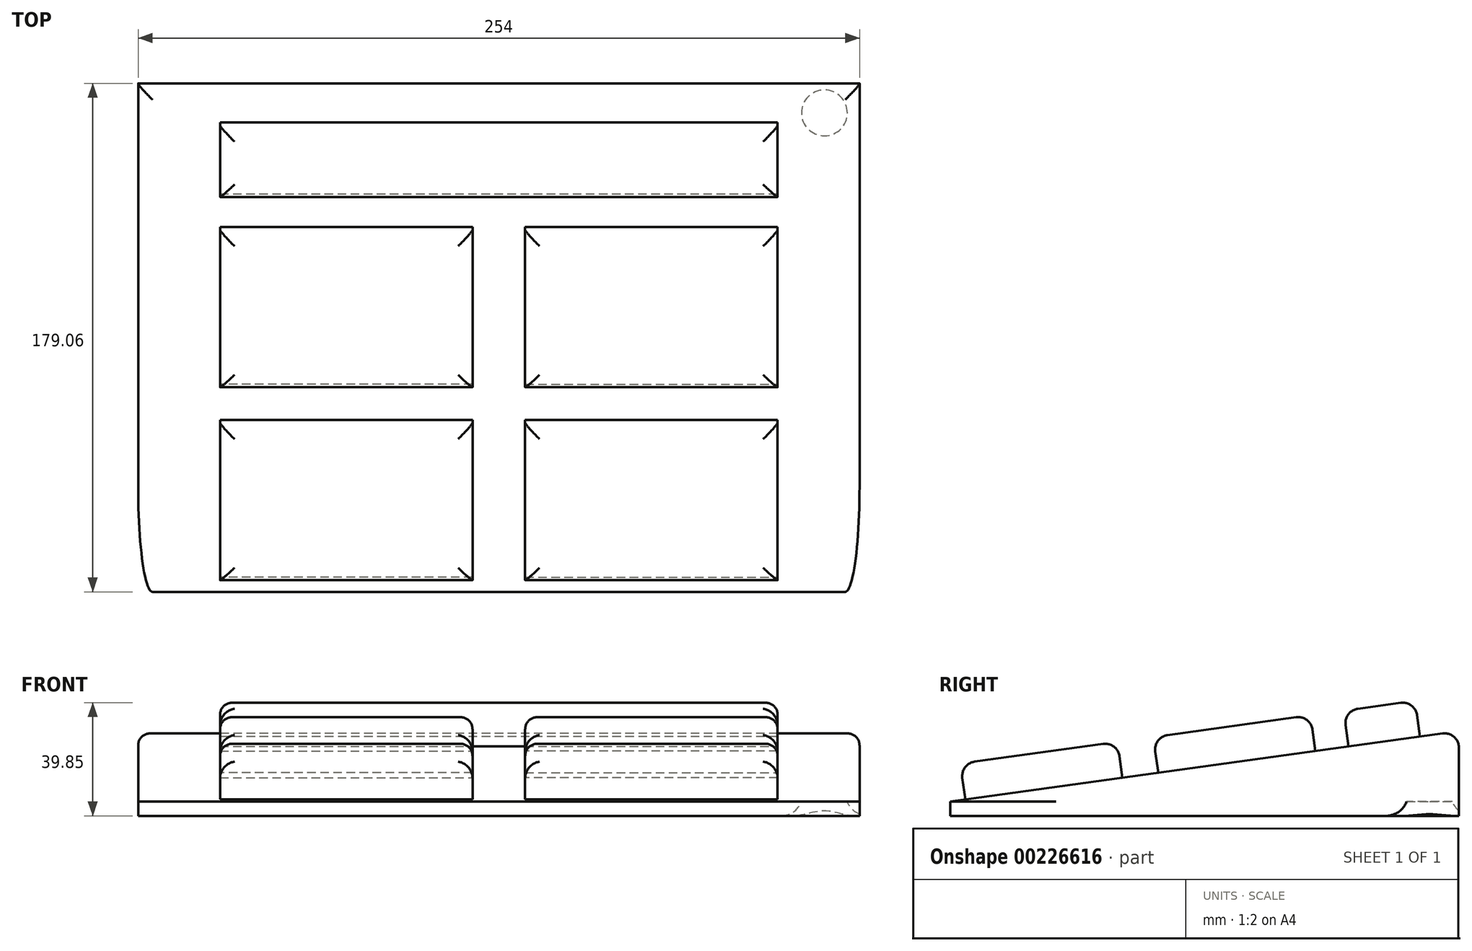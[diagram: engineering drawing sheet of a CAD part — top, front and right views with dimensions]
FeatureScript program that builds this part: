
annotation { "Feature Type Name" : "Feature", "Feature Type Description" : "" }
export const myFeature = defineFeature(function(context is Context, id is Id, definition is map)
    precondition{}
    {
        {
            var Q0;
            Q0=qCreatedBy(makeId("Right.planeOp"),FACE);
            var sketch = newSketch(context, id + "F0", { "sketchPlane" : qUnion([Q0])});
            skLineSegment(sketch, "E0", {"start": v(102.27, 24.73) * mm, "end": v(102.27, 0) * mm});
            skLineSegment(sketch, "E1", {"start": v(102.27, 0) * mm, "end": v(-76.8, 0) * mm});
            skLineSegment(sketch, "E2", {"start": v(-76.8, 0) * mm, "end": v(102.27, 24.73) * mm});
            skSolve(sketch);
        }
        {
            var Q0;
            Q0 = qSketchRegion(id + "F0", true);
            extrude(context, id + "F1", {"entities" : qUnion([Q0]), "endBound" : BoundingType.SYMMETRIC, "depth" : 254 * mm});
        }
        {
            var Q0;
            Q0=makeQuery(id+"F1.opExtrude","CAP_EDGE",EDGE,{"disambiguationData":[OSD([sQuery(id+"F0.wireOp",EDGE,"E2")])],"isStart":true});
            var Q1;
            Q1=makeQuery(id+"F1.opExtrude","CAP_EDGE",EDGE,{"disambiguationData":[OSD([sQuery(id+"F0.wireOp",EDGE,"E2")])],"isStart":false});
            var Q2;
            Q2=makeQuery(id+"F1.opExtrude","SWEPT_EDGE",EDGE,{"disambiguationData":[OSD([sQuery(id+"F0.wireOp",EDGE,"E0"),sQuery(id+"F0.wireOp",EDGE,"E2")])]});
            fillet(context, id + "F2", {"entities" : qUnion([Q0, Q1, Q2]), "radius" : 5.08 * mm, "tangentPropagation" : true, "allowEdgeOverflow" : false});
        }
        {
            var Q0;
            Q0=makeQuery(id+"F1.opExtrude","SWEPT_FACE",FACE,{"disambiguationData":[OSD([sQuery(id+"F0.wireOp",EDGE,"E2")])]});
            var sketch = newSketch(context, id + "F3", { "sketchPlane" : qUnion([Q0])});
            skLineSegment(sketch, "E3", {"start": v(0, 62.96) * mm, "end": v(0, -67.39) * mm, "construction": true});
            skLineSegment(sketch, "E4", {"start": v(-9.26, -2.21) * mm, "end": v(-98.16, -2.21) * mm});
            skPoint(sketch, "E4.startSnap0", {"position": v(0, -2.21) * mm});
            skLineSegment(sketch, "E5", {"start": v(-98.16, -2.21) * mm, "end": v(-98.16, 53.67) * mm});
            skLineSegment(sketch, "E6", {"start": v(-98.16, 53.67) * mm, "end": v(-9.26, 53.67) * mm});
            skLineSegment(sketch, "E7", {"start": v(-9.26, 53.67) * mm, "end": v(-9.26, -2.21) * mm});
            skLineSegment(sketch, "E8", {"start": v(-98.16, -14.91) * mm, "end": v(-9.26, -14.91) * mm});
            skLineSegment(sketch, "E9", {"start": v(-9.26, -14.91) * mm, "end": v(-9.26, -70.8) * mm});
            skLineSegment(sketch, "E10", {"start": v(-9.26, -70.8) * mm, "end": v(-98.16, -70.8) * mm});
            skLineSegment(sketch, "E11", {"start": v(-98.16, -70.8) * mm, "end": v(-98.16, -14.91) * mm});
            skLineSegment(sketch, "E12.MirrorCS", {"start": v(98.16, -2.21) * mm, "end": v(98.16, 53.67) * mm});
            skLineSegment(sketch, "E13.MirrorCS", {"start": v(98.16, 53.67) * mm, "end": v(9.26, 53.67) * mm});
            skLineSegment(sketch, "E14.MirrorCS", {"start": v(9.26, 53.67) * mm, "end": v(9.26, -2.21) * mm});
            skLineSegment(sketch, "E15.MirrorCS", {"start": v(9.26, -2.21) * mm, "end": v(98.16, -2.21) * mm});
            skLineSegment(sketch, "E16.MirrorCS", {"start": v(98.16, -14.91) * mm, "end": v(9.26, -14.91) * mm});
            skLineSegment(sketch, "E17.MirrorCS", {"start": v(98.16, -70.8) * mm, "end": v(98.16, -14.91) * mm});
            skLineSegment(sketch, "E18.MirrorCS", {"start": v(9.26, -70.8) * mm, "end": v(98.16, -70.8) * mm});
            skLineSegment(sketch, "E19.MirrorCS", {"start": v(9.26, -14.91) * mm, "end": v(9.26, -70.8) * mm});
            skSolve(sketch);
        }
        {
            var Q0;
            Q0=makeQuery(id+"F3.imprint","IMPRINT",FACE,{"disambiguationData":[TD([[makeQuery(id+"F3.imprint","IMPRINT",EDGE,{"derivedFrom":sQuery(id+"F3.wireOp",EDGE,"E4")}),-1.0]])]});
            var Q1;
            Q1=makeQuery(id+"F3.imprint","IMPRINT",FACE,{"disambiguationData":[TD([[makeQuery(id+"F3.imprint","IMPRINT",EDGE,{"derivedFrom":sQuery(id+"F3.wireOp",EDGE,"E12.MirrorCS")}),1.0]])]});
            var Q2;
            Q2=makeQuery(id+"F3.imprint","IMPRINT",FACE,{"disambiguationData":[TD([[makeQuery(id+"F3.imprint","IMPRINT",EDGE,{"derivedFrom":sQuery(id+"F3.wireOp",EDGE,"E16.MirrorCS")}),1.0]])]});
            var Q3;
            Q3=makeQuery(id+"F3.imprint","IMPRINT",FACE,{"disambiguationData":[TD([[makeQuery(id+"F3.imprint","IMPRINT",EDGE,{"derivedFrom":sQuery(id+"F3.wireOp",EDGE,"E8")}),-1.0]])]});
            extrude(context, id + "F4", {"entities" : qUnion([Q0, Q1, Q2, Q3]), "operationType" : NewBodyOperationType.ADD, "depth" : 12.7 * mm});
        }
        {
            var Q0;
            Q0=makeQuery(id+"F4.opExtrude","CAP_EDGE",EDGE,{"disambiguationData":[OSD([sQuery(id+"F3.wireOp",EDGE,"E5")])],"isStart":false});
            var Q1;
            Q1=makeQuery(id+"F4.opExtrude","CAP_EDGE",EDGE,{"disambiguationData":[OSD([sQuery(id+"F3.wireOp",EDGE,"E4")])],"isStart":false});
            var Q2;
            Q2=makeQuery(id+"F4.opExtrude","CAP_EDGE",EDGE,{"disambiguationData":[OSD([sQuery(id+"F3.wireOp",EDGE,"E11")])],"isStart":false});
            var Q3;
            Q3=makeQuery(id+"F4.opExtrude","CAP_EDGE",EDGE,{"disambiguationData":[OSD([sQuery(id+"F3.wireOp",EDGE,"E10")])],"isStart":false});
            var Q4;
            Q4=makeQuery(id+"F4.opExtrude","CAP_EDGE",EDGE,{"disambiguationData":[OSD([sQuery(id+"F3.wireOp",EDGE,"E8")])],"isStart":false});
            var Q5;
            Q5=makeQuery(id+"F4.opExtrude","CAP_EDGE",EDGE,{"disambiguationData":[OSD([sQuery(id+"F3.wireOp",EDGE,"E9")])],"isStart":false});
            var Q6;
            Q6=makeQuery(id+"F4.opExtrude","CAP_EDGE",EDGE,{"disambiguationData":[OSD([sQuery(id+"F3.wireOp",EDGE,"E15.MirrorCS")])],"isStart":false});
            var Q7;
            Q7=makeQuery(id+"F4.opExtrude","CAP_EDGE",EDGE,{"disambiguationData":[OSD([sQuery(id+"F3.wireOp",EDGE,"E14.MirrorCS")])],"isStart":false});
            var Q8;
            Q8=makeQuery(id+"F4.opExtrude","CAP_EDGE",EDGE,{"disambiguationData":[OSD([sQuery(id+"F3.wireOp",EDGE,"E13.MirrorCS")])],"isStart":false});
            var Q9;
            Q9=makeQuery(id+"F4.opExtrude","CAP_EDGE",EDGE,{"disambiguationData":[OSD([sQuery(id+"F3.wireOp",EDGE,"E12.MirrorCS")])],"isStart":false});
            var Q10;
            Q10=makeQuery(id+"F4.opExtrude","CAP_EDGE",EDGE,{"disambiguationData":[OSD([sQuery(id+"F3.wireOp",EDGE,"E16.MirrorCS")])],"isStart":false});
            var Q11;
            Q11=makeQuery(id+"F4.opExtrude","CAP_FACE",FACE,{"disambiguationData":[OSD([sQuery(id+"F3.wireOp",EDGE,"E16.MirrorCS"),sQuery(id+"F3.wireOp",EDGE,"E17.MirrorCS"),sQuery(id+"F3.wireOp",EDGE,"E18.MirrorCS"),sQuery(id+"F3.wireOp",EDGE,"E19.MirrorCS")])],"isStart":false});
            var Q12;
            Q12=makeQuery(id+"F4.opExtrude","CAP_EDGE",EDGE,{"disambiguationData":[OSD([sQuery(id+"F3.wireOp",EDGE,"E17.MirrorCS")])],"isStart":false});
            var Q13;
            Q13=makeQuery(id+"F4.opExtrude","CAP_EDGE",EDGE,{"disambiguationData":[OSD([sQuery(id+"F3.wireOp",EDGE,"E18.MirrorCS")])],"isStart":false});
            var Q14;
            Q14=makeQuery(id+"F4.opExtrude","CAP_EDGE",EDGE,{"disambiguationData":[OSD([sQuery(id+"F3.wireOp",EDGE,"E7")])],"isStart":false});
            var Q15;
            Q15=makeQuery(id+"F4.opExtrude","CAP_EDGE",EDGE,{"disambiguationData":[OSD([sQuery(id+"F3.wireOp",EDGE,"E6")])],"isStart":false});
            fillet(context, id + "F5", {"entities" : qUnion([Q0, Q1, Q2, Q3, Q4, Q5, Q6, Q7, Q8, Q9, Q10, Q11, Q12, Q13, Q14, Q15]), "radius" : 5.08 * mm, "tangentPropagation" : true, "allowEdgeOverflow" : false});
        }
        {
            var Q0;
            Q0=makeQuery(id+"F1.opExtrude","SWEPT_FACE",FACE,{"disambiguationData":[OSD([sQuery(id+"F0.wireOp",EDGE,"E2")])]});
            var sketch = newSketch(context, id + "F6", { "sketchPlane" : qUnion([Q0])});
            skLineSegment(sketch, "E20", {"start": v(-98.16, 65.43) * mm, "end": v(98.16, 65.43) * mm});
            skLineSegment(sketch, "E21", {"start": v(98.16, 65.43) * mm, "end": v(98.16, 90.83) * mm});
            skLineSegment(sketch, "E22", {"start": v(98.16, 90.83) * mm, "end": v(-98.16, 90.83) * mm});
            skLineSegment(sketch, "E23", {"start": v(-98.16, 90.83) * mm, "end": v(-98.16, 65.43) * mm});
            skSolve(sketch);
        }
        {
            var Q0;
            Q0 = qSketchRegion(id + "F6", true);
            extrude(context, id + "F7", {"entities" : qUnion([Q0]), "operationType" : NewBodyOperationType.ADD, "depth" : 12.7 * mm});
        }
        {
            var Q0;
            Q0=makeQuery(id+"F7.opExtrude","CAP_EDGE",EDGE,{"disambiguationData":[OSD([sQuery(id+"F6.wireOp",EDGE,"E20")])],"isStart":false});
            var Q1;
            Q1=makeQuery(id+"F7.opExtrude","CAP_EDGE",EDGE,{"disambiguationData":[OSD([sQuery(id+"F6.wireOp",EDGE,"E22")])],"isStart":false});
            var Q2;
            Q2=makeQuery(id+"F7.opExtrude","CAP_EDGE",EDGE,{"disambiguationData":[OSD([sQuery(id+"F6.wireOp",EDGE,"E21")])],"isStart":false});
            var Q3;
            Q3=makeQuery(id+"F7.opExtrude","CAP_EDGE",EDGE,{"disambiguationData":[OSD([sQuery(id+"F6.wireOp",EDGE,"E23")])],"isStart":false});
            fillet(context, id + "F8", {"entities" : qUnion([Q0, Q1, Q2, Q3]), "radius" : 5.08 * mm, "tangentPropagation" : true, "allowEdgeOverflow" : false});
        }
        {
            var Q0;
            Q0=makeQuery(id+"F1.opExtrude","SWEPT_FACE",FACE,{"disambiguationData":[OSD([sQuery(id+"F0.wireOp",EDGE,"E1")])]});
            var sketch = newSketch(context, id + "F9", { "sketchPlane" : qUnion([Q0])});
            skLineSegment(sketch, "E24", {"start": v(0, 52.16) * mm, "end": v(0, -99.77) * mm, "construction": true});
            skPoint(sketch, "E24.endSnap0", {"position": v(0, -102.27) * mm});
            skCircle(sketch, "E25", {"center": v(-114.62, -91.88) * mm, "radius": 8.07 * mm});
            skCircle(sketch, "E26.MirrorC", {"center": v(114.62, -91.88) * mm, "radius": 8.07 * mm});
            skSolve(sketch);
        }
        {
            var Q0;
            Q0=makeQuery(id+"F9.imprint","IMPRINT",FACE,{"disambiguationData":[TD([[makeQuery(id+"F9.imprint","IMPRINT",EDGE,{"derivedFrom":sQuery(id+"F9.wireOp",EDGE,"E25")}),1.0]])]});
            var Q1;
            Q1=makeQuery(id+"F9.imprint","IMPRINT",FACE,{"disambiguationData":[TD([[makeQuery(id+"F9.imprint","IMPRINT",EDGE,{"derivedFrom":sQuery(id+"F9.wireOp",EDGE,"E26.MirrorC")}),-1.0]])]});
            extrude(context, id + "F10", {"entities" : qUnion([Q0, Q1]), "operationType" : NewBodyOperationType.ADD, "depth" : 5.08 * mm});
        }
        {
            var Q0;
            Q0=makeQuery(id+"F10.opExtrude","CAP_EDGE",EDGE,{"disambiguationData":[OSD([sQuery(id+"F9.wireOp",EDGE,"E26.MirrorC")])],"isStart":false});
            var Q1;
            Q1=makeQuery(id+"F10.opExtrude","CAP_EDGE",EDGE,{"disambiguationData":[OSD([sQuery(id+"F9.wireOp",EDGE,"E25")])],"isStart":false});
            fillet(context, id + "F11", {"entities" : qUnion([Q0, Q1]), "radius" : 7.62 * mm, "tangentPropagation" : true, "allowEdgeOverflow" : false});
        }
    });
